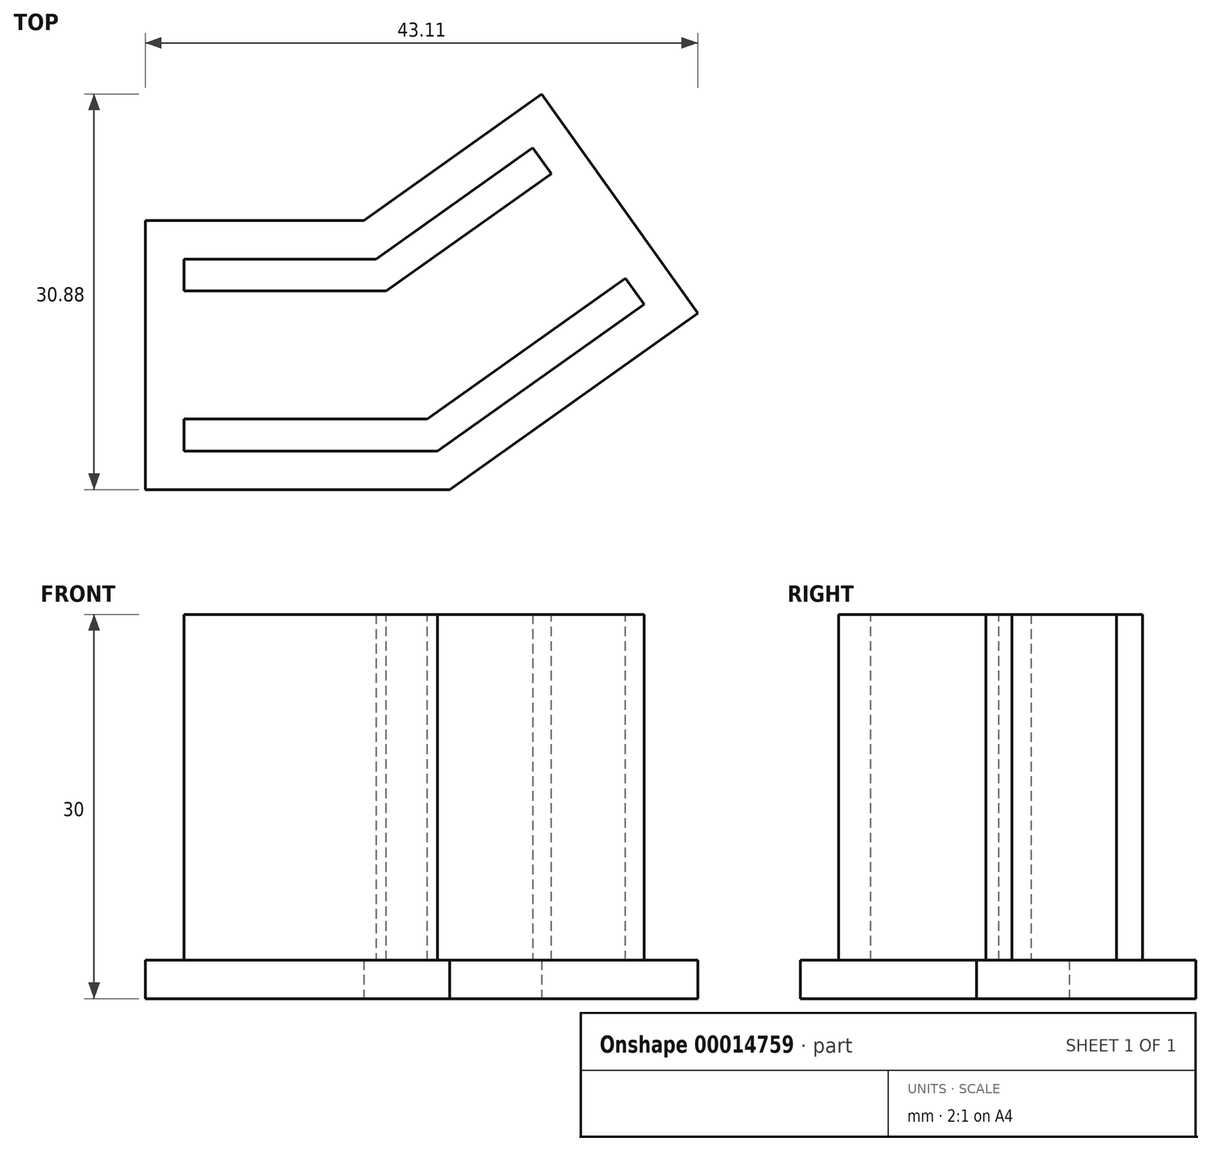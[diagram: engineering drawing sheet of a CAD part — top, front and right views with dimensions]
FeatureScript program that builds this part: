
annotation { "Feature Type Name" : "Feature", "Feature Type Description" : "" }
export const myFeature = defineFeature(function(context is Context, id is Id, definition is map)
    precondition{}
    {
        {
            var Q0;
            Q0=qCreatedBy(makeId("Top.planeOp"),FACE);
            var sketch = newSketch(context, id + "F0", { "sketchPlane" : qUnion([Q0])});
            skLineSegment(sketch, "E0", {"start": v(-21.88, 3.11) * mm, "end": v(-6.88, 3.11) * mm});
            skLineSegment(sketch, "E1", {"start": v(-6.88, 3.11) * mm, "end": v(5.35, 11.8) * mm});
            skLineSegment(sketch, "E2", {"start": v(5.35, 11.8) * mm, "end": v(14.04, -0.42) * mm});
            skLineSegment(sketch, "E3", {"start": v(-21.88, 3.11) * mm, "end": v(-21.88, -11.89) * mm});
            skLineSegment(sketch, "E4", {"start": v(14.04, -0.42) * mm, "end": v(-2.09, -11.89) * mm});
            skLineSegment(sketch, "E5", {"start": v(-2.09, -11.89) * mm, "end": v(-21.88, -11.89) * mm});
            skLineSegment(sketch, "E6", {"start": v(6.05, 16) * mm, "end": v(-7.83, 6.11) * mm});
            skLineSegment(sketch, "E7", {"start": v(-7.83, 6.11) * mm, "end": v(-24.88, 6.11) * mm});
            skLineSegment(sketch, "E8", {"start": v(-24.88, 6.11) * mm, "end": v(-24.88, -14.89) * mm});
            skLineSegment(sketch, "E9", {"start": v(-24.88, -14.89) * mm, "end": v(-1.13, -14.89) * mm});
            skLineSegment(sketch, "E10", {"start": v(-1.13, -14.89) * mm, "end": v(18.23, -1.12) * mm});
            skLineSegment(sketch, "E11", {"start": v(6.05, 16) * mm, "end": v(18.23, -1.12) * mm});
            skSolve(sketch);
        }
        {
            var Q0;
            Q0=makeQuery(id+"F0.imprint","IMPRINT",FACE,{"disambiguationData":[TD([[makeQuery(id+"F0.imprint","IMPRINT",EDGE,{"derivedFrom":sQuery(id+"F0.wireOp",EDGE,"E0")}),-1.0]])]});
            extrude(context, id + "F1", {"entities" : qUnion([Q0]), "depth" : 30 * mm});
        }
        {
            var Q0;
            Q0=makeQuery(id+"F1.opExtrude","CAP_FACE",FACE,{"disambiguationData":[OSD([sQuery(id+"F0.wireOp",EDGE,"E0"),sQuery(id+"F0.wireOp",EDGE,"E1"),sQuery(id+"F0.wireOp",EDGE,"E2"),sQuery(id+"F0.wireOp",EDGE,"E3"),sQuery(id+"F0.wireOp",EDGE,"E4"),sQuery(id+"F0.wireOp",EDGE,"E5")])],"isStart":false});
            var sketch = newSketch(context, id + "F2", { "sketchPlane" : qUnion([Q0])});
            skLineSegment(sketch, "E12", {"start": v(-21.88, 0.61) * mm, "end": v(-6.08, 0.61) * mm});
            skLineSegment(sketch, "E13", {"start": v(6.8, 9.77) * mm, "end": v(-6.08, 0.61) * mm});
            skLineSegment(sketch, "E14", {"start": v(12.6, 1.62) * mm, "end": v(-2.88, -9.39) * mm});
            skLineSegment(sketch, "E15", {"start": v(-21.88, -9.39) * mm, "end": v(-2.88, -9.39) * mm});
            skLineSegment(sketch, "E16", {"start": v(-21.88, 0.61) * mm, "end": v(-21.88, -9.39) * mm});
            skLineSegment(sketch, "E17", {"start": v(6.8, 9.77) * mm, "end": v(12.6, 1.62) * mm});
            skSolve(sketch);
        }
        {
            var Q0;
            Q0=makeQuery(id+"F2.imprint","IMPRINT",FACE,{"disambiguationData":[TD([[makeQuery(id+"F2.imprint","IMPRINT",EDGE,{"derivedFrom":sQuery(id+"F2.wireOp",EDGE,"E12")}),-1.0]])]});
            extrude(context, id + "F3", {"entities" : qUnion([Q0]), "operationType" : NewBodyOperationType.REMOVE, "oppositeDirection" : true, "depth" : 27 * mm});
        }
        {
            var Q0;
            Q0=makeQuery(id+"F0.imprint","IMPRINT",FACE,{"disambiguationData":[TD([[makeQuery(id+"F0.imprint","IMPRINT",EDGE,{"derivedFrom":sQuery(id+"F0.wireOp",EDGE,"E0")}),1.0]])]});
            extrude(context, id + "F4", {"entities" : qUnion([Q0]), "operationType" : NewBodyOperationType.ADD, "depth" : 3 * mm});
        }
    });
